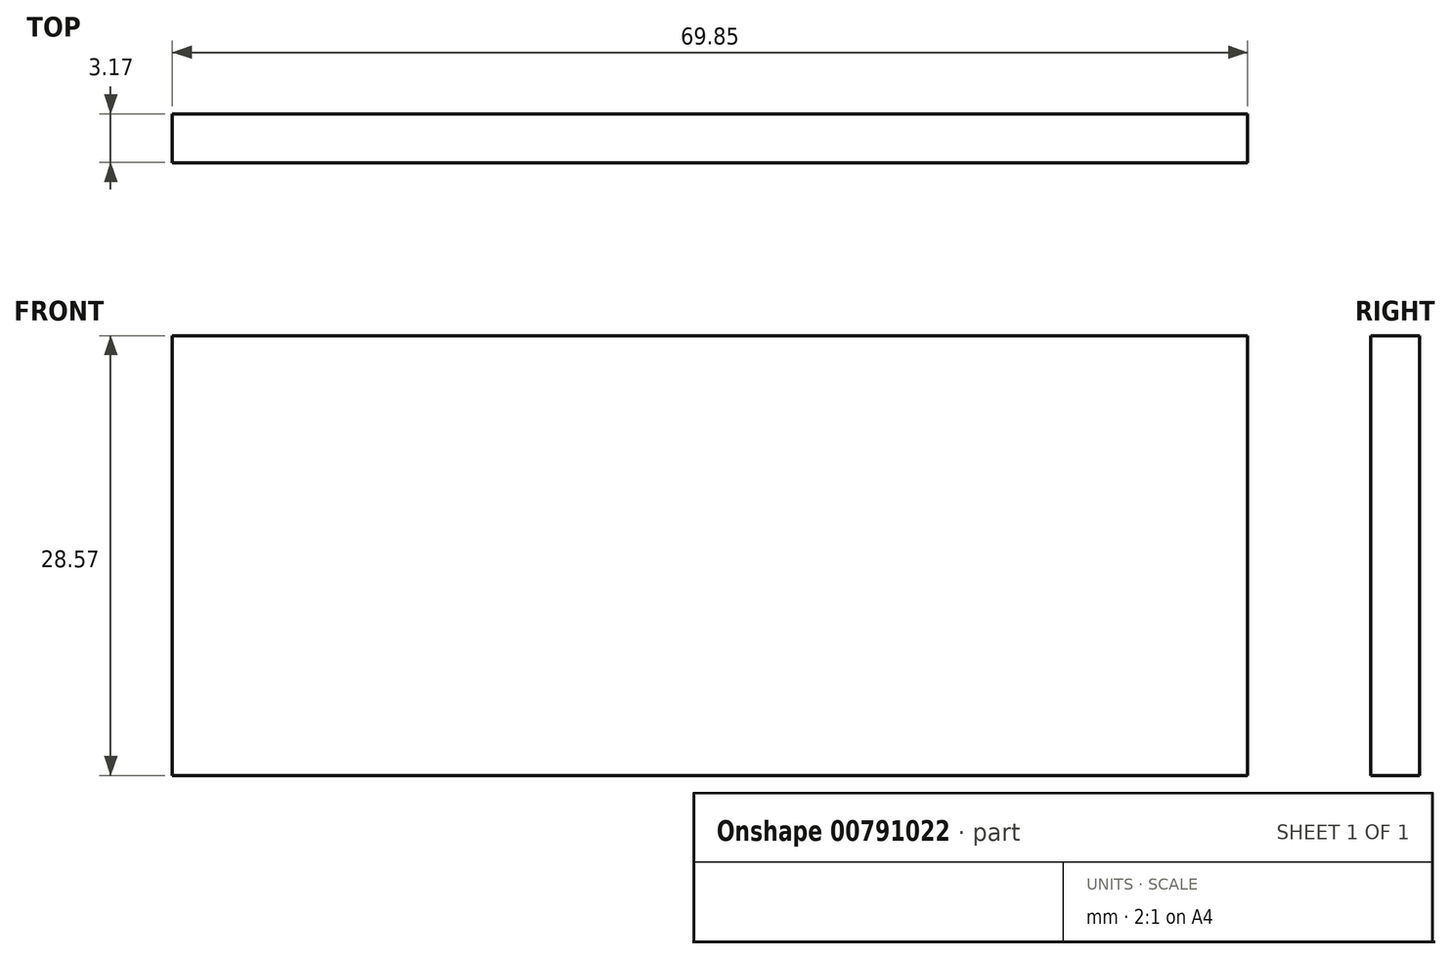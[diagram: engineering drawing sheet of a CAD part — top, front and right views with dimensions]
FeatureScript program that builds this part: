
annotation { "Feature Type Name" : "Feature", "Feature Type Description" : "" }
export const myFeature = defineFeature(function(context is Context, id is Id, definition is map)
    precondition{}
    {
        {
            var Q0;
            Q0=qCreatedBy(makeId("Front.planeOp"),FACE);
            var sketch = newSketch(context, id + "F0", { "sketchPlane" : qUnion([Q0])});
            skLineSegment(sketch, "E0.bottom", {"start": v(-23.34, 13.9) * mm, "end": v(46.51, 13.9) * mm});
            skLineSegment(sketch, "E0.top", {"start": v(-23.34, -14.68) * mm, "end": v(46.51, -14.68) * mm});
            skLineSegment(sketch, "E0.left", {"start": v(-23.34, 13.9) * mm, "end": v(-23.34, -14.68) * mm});
            skLineSegment(sketch, "E0.right", {"start": v(46.51, 13.9) * mm, "end": v(46.51, -14.68) * mm});
            skSolve(sketch);
        }
        {
            var Q0;
            Q0 = qSketchRegion(id + "F0", true);
            extrude(context, id + "F1", {"entities" : qUnion([Q0]), "depth" : 3.17 * mm, "offsetDistance" : 25.4 * mm});
        }
    });
